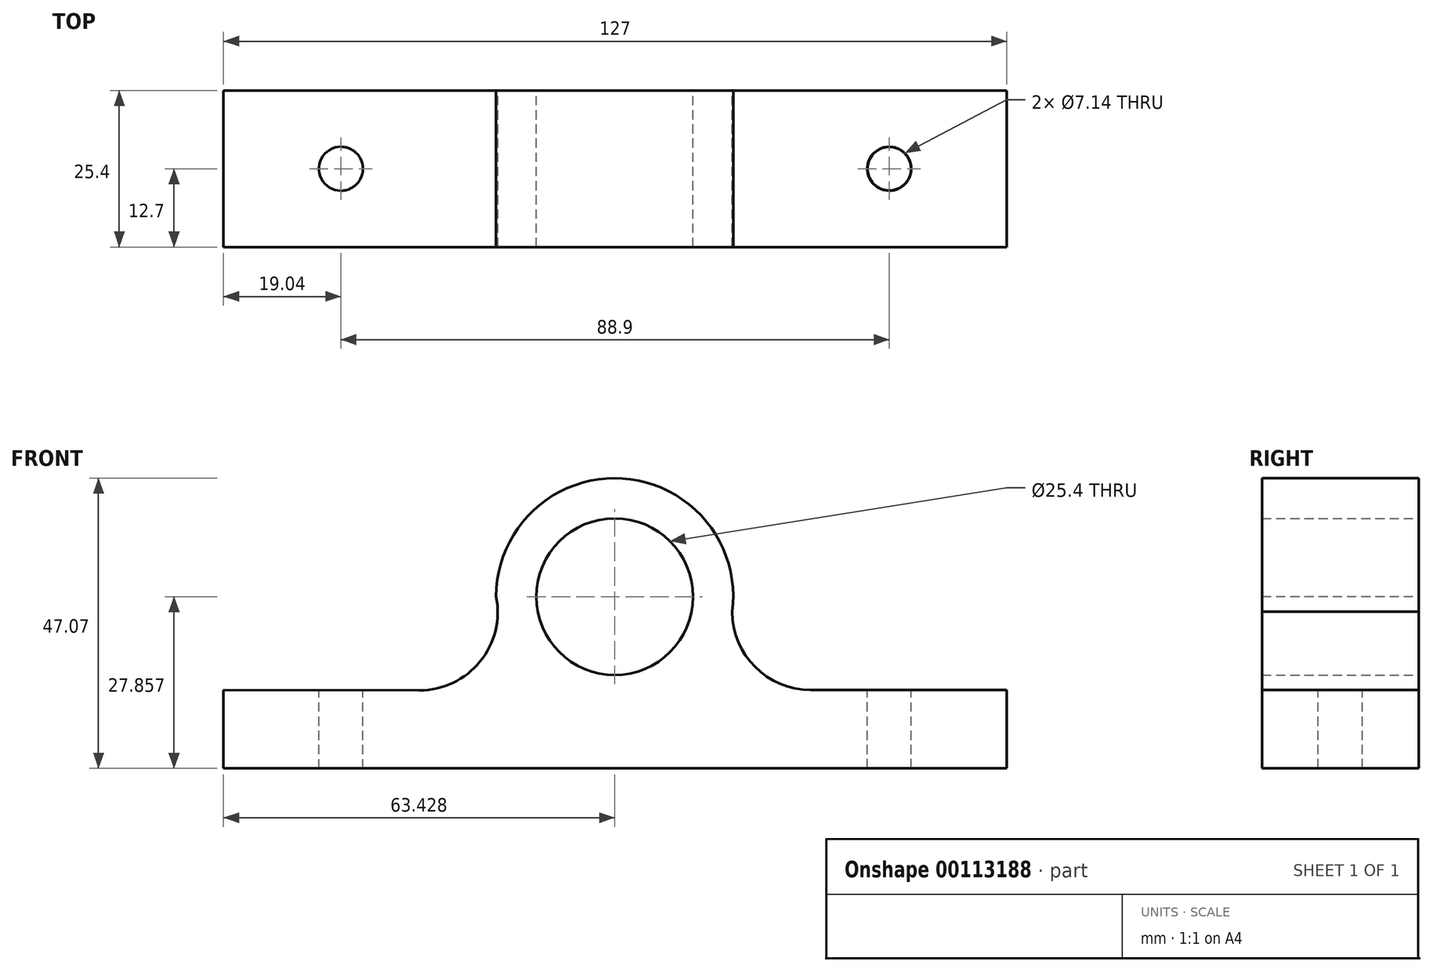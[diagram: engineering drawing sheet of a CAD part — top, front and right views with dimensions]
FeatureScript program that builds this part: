
annotation { "Feature Type Name" : "Feature", "Feature Type Description" : "" }
export const myFeature = defineFeature(function(context is Context, id is Id, definition is map)
    precondition{}
    {
        {
            var Q0;
            Q0=qCreatedBy(makeId("Front.planeOp"),FACE);
            var sketch = newSketch(context, id + "F0", { "sketchPlane" : qUnion([Q0])});
            skLineSegment(sketch, "E0", {"start": v(-63.36, -55.7) * mm, "end": v(63.64, -55.7) * mm});
            skLineSegment(sketch, "E1", {"start": v(-63.36, -55.7) * mm, "end": v(-63.36, -43) * mm});
            skLineSegment(sketch, "E2", {"start": v(63.64, -55.7) * mm, "end": v(63.64, -43) * mm});
            skLineSegment(sketch, "E3", {"start": v(0.14, -55.7) * mm, "end": v(0, 0) * mm});
            skPoint(sketch, "E4.visualSharp", {"position": v(0, 0) * mm});
            skLineSegment(sketch, "E5", {"start": v(-63.36, -43) * mm, "end": v(-31.6, -43.04) * mm});
            skLineSegment(sketch, "E6", {"start": v(63.64, -43) * mm, "end": v(31.81, -42.97) * mm});
            skArc(sketch, "E7.filletArc", {"start": v(-31.6, -43.04) * mm, "mid": v(-21.76, -38.38) * mm, "end": v(-19.14, -27.8) * mm});
            skArc(sketch, "E8.filletArc", {"start": v(19.12, -30.3) * mm, "mid": v(22.85, -39.26) * mm, "end": v(31.81, -42.97) * mm});
            skCircle(sketch, "E9", {"center": v(0.07, -27.85) * mm, "radius": 12.7 * mm});
            skArc(sketch, "E10", {"start": v(19.12, -30.3) * mm, "mid": v(1.32, -8.68) * mm, "end": v(-19.14, -27.8) * mm});
            skSolve(sketch);
        }
        {
            var Q0;
            Q0 = qSketchRegion(id + "F0", true);
            extrude(context, id + "F1", {"entities" : qUnion([Q0]), "depth" : 25.4 * mm});
        }
        {
            var Q0;
            Q0=makeQuery(id+"F1.opExtrude","SWEPT_FACE",FACE,{"disambiguationData":[OSD([sQuery(id+"F0.wireOp",EDGE,"E5")])]});
            var sketch = newSketch(context, id + "F2", { "sketchPlane" : qUnion([Q0])});
            skLineSegment(sketch, "E11", {"start": v(-63.32, -12.7) * mm, "end": v(-44.27, -12.7) * mm});
            skCircle(sketch, "E12", {"center": v(-44.27, -12.7) * mm, "radius": 6.35 * mm});
            skLineSegment(sketch, "E13", {"start": v(64.43, -12.7) * mm, "end": v(45.38, -12.7) * mm});
            skCircle(sketch, "E14", {"center": v(45.38, -12.7) * mm, "radius": 6.35 * mm});
            skSolve(sketch);
        }
        {
            var Q0;
            Q0=sQuery(id+"F2.wireOp",VERTEX,"E12.center");
            var Q1;
            Q1=makeQuery(id+"F1.opExtrude","SWEPT_BODY",BODY,{"disambiguationData":[OSD([sQuery(id+"F0.wireOp",EDGE,"E0"),sQuery(id+"F0.wireOp",EDGE,"E1"),sQuery(id+"F0.wireOp",EDGE,"E2"),sQuery(id+"F0.wireOp",EDGE,"E5"),sQuery(id+"F0.wireOp",EDGE,"E6"),sQuery(id+"F0.wireOp",EDGE,"E7.filletArc"),sQuery(id+"F0.wireOp",EDGE,"E8.filletArc"),sQuery(id+"F0.wireOp",EDGE,"E9"),sQuery(id+"F0.wireOp",EDGE,"E10")])]});
            hole(context, id + "F3", {"style" : HoleStyle.SIMPLE, "endStyle" : HoleEndStyle.BLIND, "holeDiameter" : 7.14 * mm, "holeDepth" : 12.7 * mm, "locations" : qUnion([Q0]), "scope" : qUnion([Q1])});
        }
        {
            var Q0;
            Q0=makeQuery(id+"F1.opExtrude","SWEPT_FACE",FACE,{"disambiguationData":[OSD([sQuery(id+"F0.wireOp",EDGE,"E6")])]});
            var sketch = newSketch(context, id + "F4", { "sketchPlane" : qUnion([Q0])});
            skLineSegment(sketch, "E15", {"start": v(63.68, -12.7) * mm, "end": v(44.63, -12.7) * mm});
            skCircle(sketch, "E16", {"center": v(44.63, -12.7) * mm, "radius": 6.35 * mm});
            skSolve(sketch);
        }
        {
            var Q0;
            Q0=sQuery(id+"F4.wireOp",VERTEX,"E15.end");
            var Q1;
            Q1=makeQuery(id+"F1.opExtrude","SWEPT_BODY",BODY,{"disambiguationData":[OSD([sQuery(id+"F0.wireOp",EDGE,"E0"),sQuery(id+"F0.wireOp",EDGE,"E1"),sQuery(id+"F0.wireOp",EDGE,"E2"),sQuery(id+"F0.wireOp",EDGE,"E5"),sQuery(id+"F0.wireOp",EDGE,"E6"),sQuery(id+"F0.wireOp",EDGE,"E7.filletArc"),sQuery(id+"F0.wireOp",EDGE,"E8.filletArc"),sQuery(id+"F0.wireOp",EDGE,"E9"),sQuery(id+"F0.wireOp",EDGE,"E10")])]});
            hole(context, id + "F5", {"style" : HoleStyle.SIMPLE, "endStyle" : HoleEndStyle.BLIND, "holeDiameter" : 7.14 * mm, "holeDepth" : 12.7 * mm, "locations" : qUnion([Q0]), "scope" : qUnion([Q1])});
        }
    });
